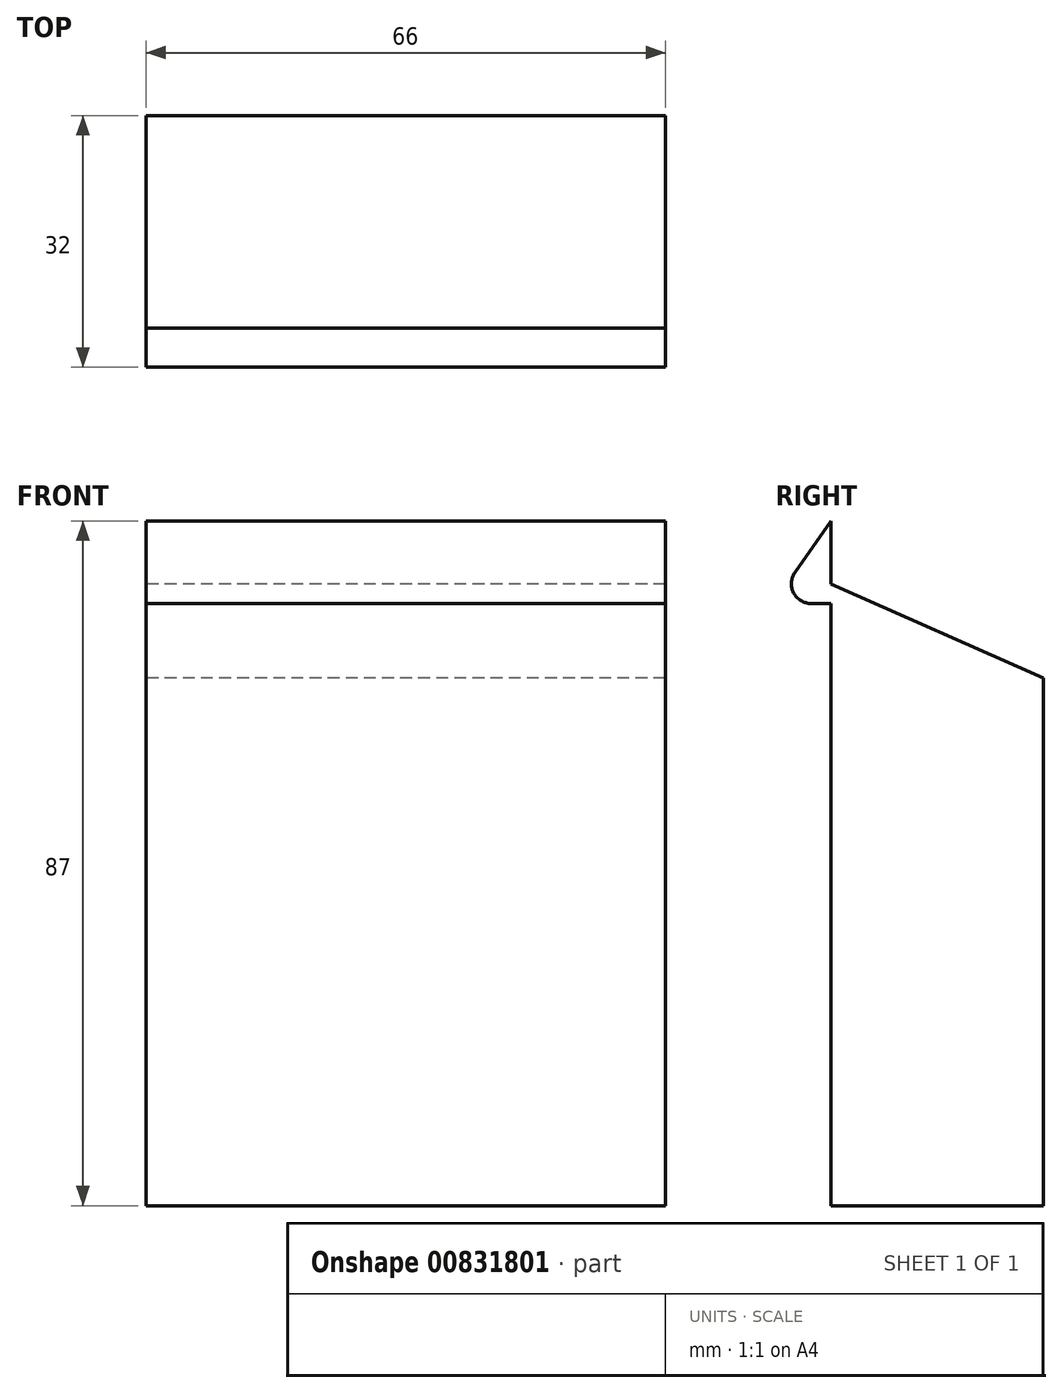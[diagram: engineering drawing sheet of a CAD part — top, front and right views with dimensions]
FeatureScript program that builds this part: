
annotation { "Feature Type Name" : "Feature", "Feature Type Description" : "" }
export const myFeature = defineFeature(function(context is Context, id is Id, definition is map)
    precondition{}
    {
        {
            var Q0;
            Q0=qCreatedBy(makeId("Front.planeOp"),FACE);
            var sketch = newSketch(context, id + "F0", { "sketchPlane" : qUnion([Q0])});
            skLineSegment(sketch, "E0.bottom", {"start": v(33, -43.5) * mm, "end": v(-33, -43.5) * mm});
            skLineSegment(sketch, "E0.top", {"start": v(33, 43.5) * mm, "end": v(-33, 43.5) * mm});
            skLineSegment(sketch, "E0.left", {"start": v(33, -43.5) * mm, "end": v(33, 43.5) * mm});
            skLineSegment(sketch, "E0.right", {"start": v(-33, -43.5) * mm, "end": v(-33, 43.5) * mm});
            skPoint(sketch, "E0.middle", {"position": v(0, 0) * mm});
            skSolve(sketch);
        }
        {
            var Q0;
            Q0=makeQuery(id+"F0.imprint","IMPRINT",FACE,{"disambiguationData":[TD([[makeQuery(id+"F0.imprint","IMPRINT",EDGE,{"derivedFrom":sQuery(id+"F0.wireOp",EDGE,"E0.bottom")}),-1.0]])]});
            extrude(context, id + "F1", {"entities" : qUnion([Q0]), "endBound" : BoundingType.SYMMETRIC, "depth" : 27 * mm, "offsetDistance" : 25 * mm});
        }
        {
            var Q0;
            Q0=makeQuery(id+"F1.opExtrude","SWEPT_FACE",FACE,{"disambiguationData":[OSD([sQuery(id+"F0.wireOp",EDGE,"E0.right")])]});
            var sketch = newSketch(context, id + "F2", { "sketchPlane" : qUnion([Q0])});
            skLineSegment(sketch, "E1", {"start": v(13.5, 43.5) * mm, "end": v(13.5, 35.5) * mm});
            skLineSegment(sketch, "E2", {"start": v(-13.5, 43.5) * mm, "end": v(-13.5, 23.5) * mm});
            skLineSegment(sketch, "E3", {"start": v(13.5, 35.5) * mm, "end": v(-13.5, 23.5) * mm});
            skLineSegment(sketch, "E4", {"start": v(-13.5, 43.5) * mm, "end": v(13.5, 43.5) * mm});
            skCircle(sketch, "E5", {"center": v(16, 35.5) * mm, "radius": 2.5 * mm});
            skLineSegment(sketch, "E6", {"start": v(16, 35.5) * mm, "end": v(13.5, 35.5) * mm, "construction": true});
            skLineSegment(sketch, "E7", {"start": v(16, 33) * mm, "end": v(13.5, 33) * mm});
            skLineSegment(sketch, "E8", {"start": v(18.06, 36.92) * mm, "end": v(13.5, 43.5) * mm});
            skSolve(sketch);
        }
        {
            var Q0;
            Q0=makeQuery(id+"F2.imprint","IMPRINT",FACE,{"disambiguationData":[TD([[makeQuery(id+"F2.imprint","IMPRINT",EDGE,{"derivedFrom":sQuery(id+"F2.wireOp",EDGE,"E1")}),1.0]])]});
            extrude(context, id + "F3", {"entities" : qUnion([Q0]), "operationType" : NewBodyOperationType.REMOVE, "oppositeDirection" : true, "depth" : 70 * mm, "offsetDistance" : 25 * mm});
        }
        {
            var Q0;
            {var subQ3=sQuery(id+"F2.wireOp",EDGE,"E7");Q0=makeQuery(id+"F2.imprint","IMPRINT",FACE,{"disambiguationData":[TD([[makeQuery(id+"F2.imprint","IMPRINT",EDGE,{"derivedFrom":subQ3}),-1.0]])]});}
            var Q1;
            {var subQ0=sQuery(id+"F2.wireOp",EDGE,"E5");var subQ3=makeQuery(id+"F2.imprint","INTERSECT",VERTEX,{"derivedFrom":[subQ0,sQuery(id+"F2.wireOp",EDGE,"E7")]});Q1=makeQuery(id+"F2.imprint","IMPRINT",FACE,{"disambiguationData":[TD([[makeQuery(id+"F2.imprint","IMPRINT",EDGE,{"disambiguationData":[TD([[subQ3,-1.0]])],"derivedFrom":subQ0}),1.0]])]});}
            var Q2;
            {var subQ0=sQuery(id+"F2.wireOp",EDGE,"E1");Q2=makeQuery(id+"F2.imprint","IMPRINT",FACE,{"disambiguationData":[TD([[makeQuery(id+"F2.imprint","IMPRINT",EDGE,{"derivedFrom":subQ0}),-1.0]])]});}
            extrude(context, id + "F4", {"entities" : qUnion([Q0, Q1, Q2]), "operationType" : NewBodyOperationType.ADD, "oppositeDirection" : true, "depth" : 66 * mm, "offsetDistance" : 25 * mm});
        }
    });
